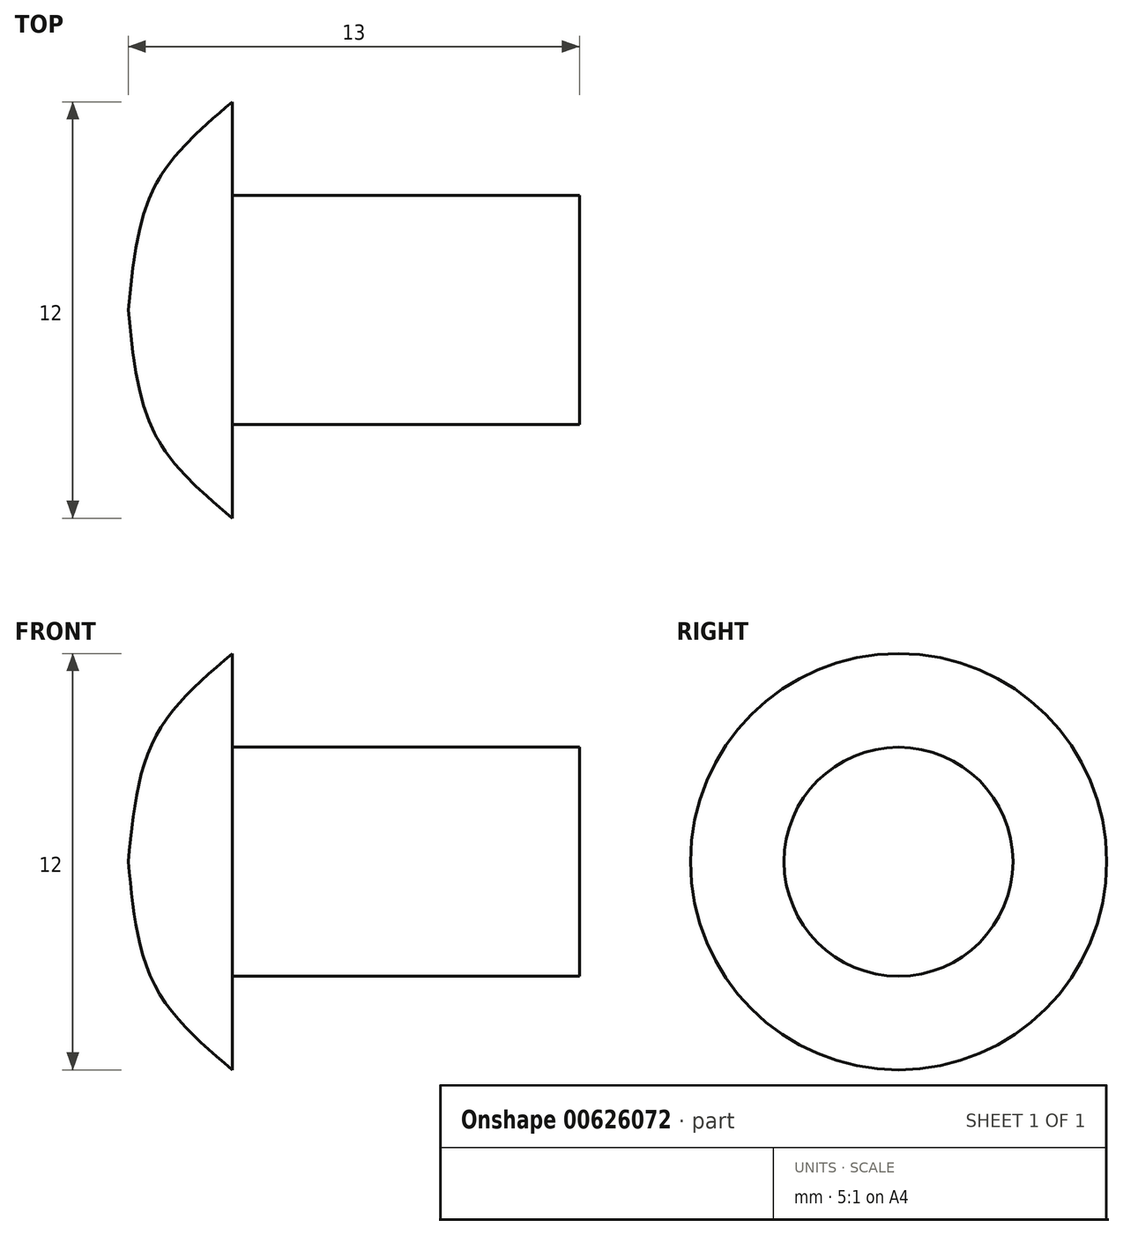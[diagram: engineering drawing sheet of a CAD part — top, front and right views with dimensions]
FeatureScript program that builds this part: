
annotation { "Feature Type Name" : "Feature", "Feature Type Description" : "" }
export const myFeature = defineFeature(function(context is Context, id is Id, definition is map)
    precondition{}
    {
        {
            var Q0;
            Q0=qCreatedBy(makeId("Front.planeOp"),FACE);
            var sketch = newSketch(context, id + "F0", { "sketchPlane" : qUnion([Q0])});
            skLineSegment(sketch, "E0", {"start": v(3, 6) * mm, "end": v(3, 3.3) * mm});
            skLineSegment(sketch, "E1", {"start": v(3, 3.3) * mm, "end": v(13, 3.3) * mm});
            skLineSegment(sketch, "E2", {"start": v(13, 3.3) * mm, "end": v(13, 0) * mm});
            skLineSegment(sketch, "E3", {"start": v(13, 0) * mm, "end": v(0, 0) * mm});
            skFitSpline(sketch, "E4", {"points": [v(3, 6) * mm, v(0.77, 3.58) * mm, v(0, 0) * mm], "startDerivative": vector(-5.32, -4.48) * mm, "endDerivative": vector(-0.72, -7.49) * mm});
            skSolve(sketch);
        }
        {
            var Q0;
            Q0=makeQuery(id+"F0.imprint","IMPRINT",FACE,{"disambiguationData":[TD([[makeQuery(id+"F0.imprint","IMPRINT",EDGE,{"derivedFrom":sQuery(id+"F0.wireOp",EDGE,"E0")}),-1.0]])]});
            var Q1;
            Q1=sQuery(id+"F0.wireOp",EDGE,"E3");
            revolve(context, id + "F1", {"surfaceOperationType" : NewSurfaceOperationType.NEW, "entities" : qUnion([Q0]), "axis" : qUnion([Q1]), "revolveType" : RevolveType.FULL});
        }
    });
